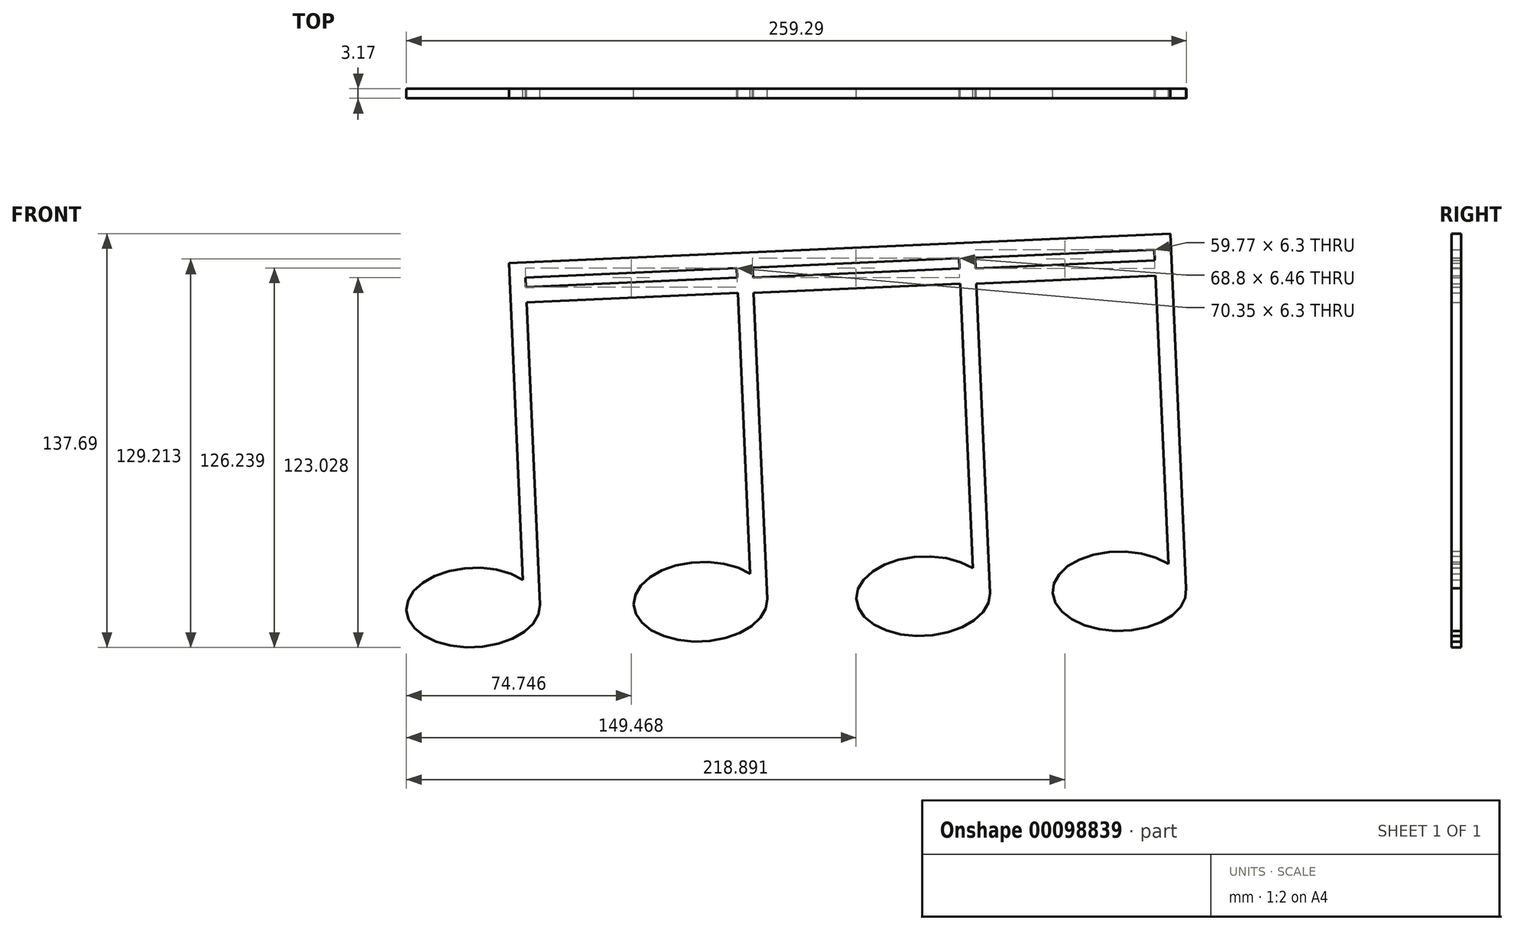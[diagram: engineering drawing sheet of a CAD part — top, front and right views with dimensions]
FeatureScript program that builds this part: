
annotation { "Feature Type Name" : "Feature", "Feature Type Description" : "" }
export const myFeature = defineFeature(function(context is Context, id is Id, definition is map)
    precondition{}
    {
        {
            var Q0;
            Q0=qCreatedBy(makeId("Front.planeOp"),FACE);
            var sketch = newSketch(context, id + "F0", { "sketchPlane" : qUnion([Q0])});
            skEllipticalArc(sketch, "E0", {});
            skEllipticalArc(sketch, "E1", {});
            skEllipticalArc(sketch, "E2", {});
            skEllipticalArc(sketch, "E3", {});
            skLineSegment(sketch, "E4", {"start": v(83.57, 2.37) * mm, "end": v(78.32, 120.33) * mm});
            skLineSegment(sketch, "E5", {"start": v(78.32, 120.33) * mm, "end": v(-141.6, 110.53) * mm});
            skLineSegment(sketch, "E6", {"start": v(-141.6, 110.53) * mm, "end": v(-136.9, 5.17) * mm});
            skLineSegment(sketch, "E7", {"start": v(-135.73, 97.44) * mm, "end": v(-131.25, -3.17) * mm});
            skLineSegment(sketch, "E8", {"start": v(-61.36, 7.13) * mm, "end": v(-65.52, 100.57) * mm});
            skLineSegment(sketch, "E9", {"start": v(-55.69, -1.2) * mm, "end": v(-60.22, 100.57) * mm});
            skLineSegment(sketch, "E10", {"start": v(12.64, 9) * mm, "end": v(8.42, 103.63) * mm});
            skLineSegment(sketch, "E11", {"start": v(18.3, 0.68) * mm, "end": v(13.72, 103.63) * mm});
            skLineSegment(sketch, "E12", {"start": v(77.6, 10.5) * mm, "end": v(73.33, 106.29) * mm});
            skLineSegment(sketch, "E13", {"start": v(-135.73, 97.44) * mm, "end": v(-65.52, 100.57) * mm});
            skLineSegment(sketch, "E14", {"start": v(-60.22, 100.57) * mm, "end": v(8.42, 103.63) * mm});
            skLineSegment(sketch, "E15", {"start": v(13.72, 103.63) * mm, "end": v(73.33, 106.29) * mm});
            skLineSegment(sketch, "E16", {"start": v(-135.96, 102.52) * mm, "end": v(-136.1, 105.69) * mm});
            skLineSegment(sketch, "E17", {"start": v(-136.1, 105.69) * mm, "end": v(-65.9, 108.82) * mm});
            skLineSegment(sketch, "E18", {"start": v(-65.9, 108.82) * mm, "end": v(-65.75, 105.65) * mm});
            skLineSegment(sketch, "E19", {"start": v(-65.75, 105.65) * mm, "end": v(-135.96, 102.52) * mm});
            skLineSegment(sketch, "E20", {"start": v(-60.45, 105.65) * mm, "end": v(-60.6, 109.05) * mm});
            skLineSegment(sketch, "E21", {"start": v(-60.6, 109.05) * mm, "end": v(8.04, 112.11) * mm});
            skLineSegment(sketch, "E22", {"start": v(8.04, 112.11) * mm, "end": v(8.2, 108.7) * mm});
            skLineSegment(sketch, "E23", {"start": v(8.2, 108.7) * mm, "end": v(-60.45, 105.65) * mm});
            skLineSegment(sketch, "E24", {"start": v(13.5, 108.7) * mm, "end": v(73.1, 111.36) * mm});
            skLineSegment(sketch, "E25", {"start": v(73.1, 111.36) * mm, "end": v(72.95, 115) * mm});
            skLineSegment(sketch, "E26", {"start": v(72.95, 115) * mm, "end": v(13.33, 112.35) * mm});
            skLineSegment(sketch, "E27", {"start": v(13.33, 112.35) * mm, "end": v(13.5, 108.7) * mm});
            const initialGuessF0  = {"E0": [-0.07789188743155874, -0.0021895567782876375, -0.9990091731631708, -0.04450474059960402, 0.022225, 0.013229209000000006, 3.846425726231439, 3.141592653589793], "E1": [-0.0038939269808720305, -0.00030941677834428255, -0.9990091731631707, -0.04450474059960405, 0.022225, 0.013229209000000006, 3.8464257262314394, 3.141592653589793], "E2": [-0.15345324939867522, -0.0041094196801746445, 0.9991412671940452, 0.04143341875681539, 0.022225, 0.013233400000000005, 0.7057906602020476, 0.0015783246104190578], "E3": [0.06139828080831473, 0.0013495274790572681, 0.9999673938294242, 0.008075350022700826, 0.022225, 0.013233400000000005, 0.7489924792192049, 0.06392307777555]};
            skSetInitialGuess(sketch, initialGuessF0);
            skSolve(sketch);
        }
        {
            var Q0;
            Q0 = qSketchRegion(id + "F0", true);
            extrude(context, id + "F1", {"entities" : qUnion([Q0]), "depth" : 3.17 * mm});
        }
    });
